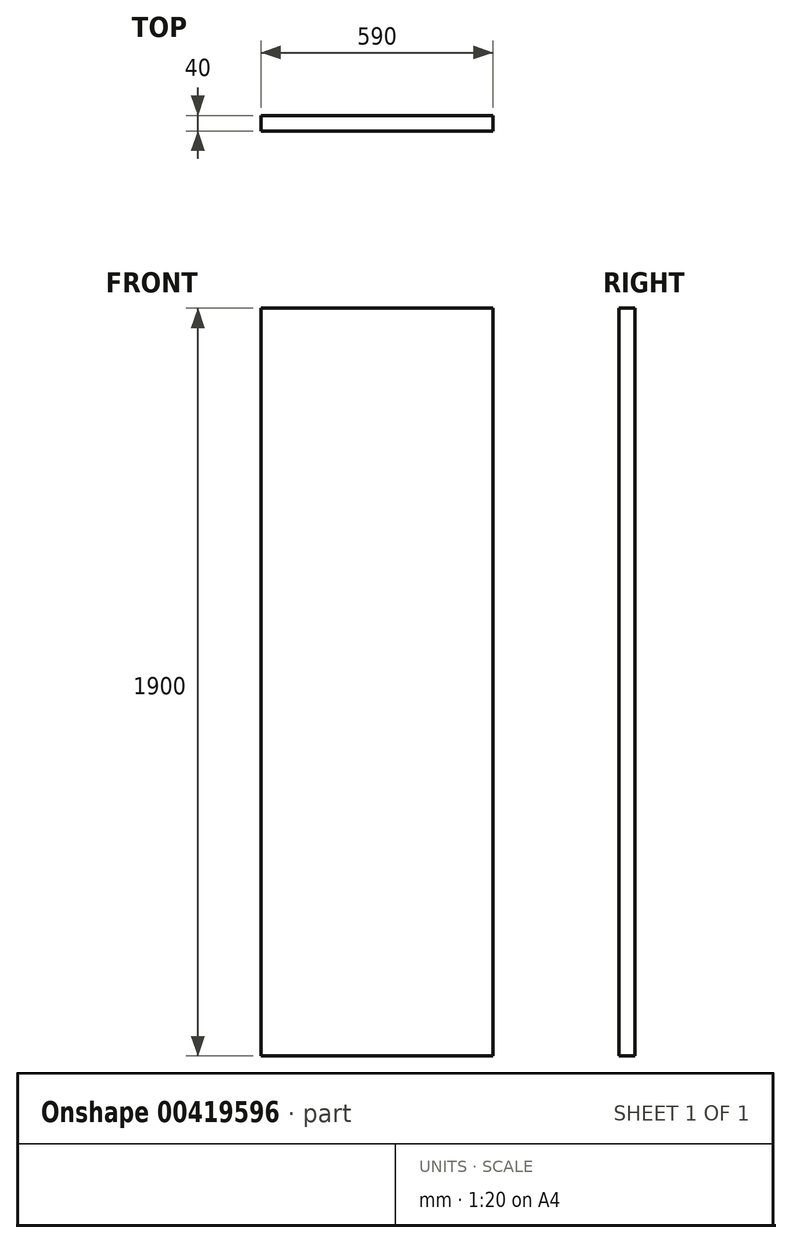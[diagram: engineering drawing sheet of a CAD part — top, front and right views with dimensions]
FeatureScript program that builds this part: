
annotation { "Feature Type Name" : "Feature", "Feature Type Description" : "" }
export const myFeature = defineFeature(function(context is Context, id is Id, definition is map)
    precondition{}
    {
        {
            var Q0;
            Q0=qCreatedBy(makeId("Top.planeOp"),FACE);
            var sketch = newSketch(context, id + "F0", { "sketchPlane" : qUnion([Q0])});
            skLineSegment(sketch, "E0.bottom", {"start": v(-499.2, 10.74) * mm, "end": v(90.8, 10.74) * mm});
            skLineSegment(sketch, "E0.top", {"start": v(-499.2, -29.26) * mm, "end": v(90.8, -29.26) * mm});
            skLineSegment(sketch, "E0.left", {"start": v(-499.2, 10.74) * mm, "end": v(-499.2, -29.26) * mm});
            skLineSegment(sketch, "E0.right", {"start": v(90.8, 10.74) * mm, "end": v(90.8, -29.26) * mm});
            skSolve(sketch);
        }
        {
            var Q0;
            Q0=makeQuery(id+"F0.imprint","IMPRINT",FACE,{"disambiguationData":[TD([[makeQuery(id+"F0.imprint","IMPRINT",EDGE,{"derivedFrom":sQuery(id+"F0.wireOp",EDGE,"E0.bottom")}),-1.0]])]});
            extrude(context, id + "F1", {"entities" : qUnion([Q0]), "depth" : 1900 * mm});
        }
    });
